FCSTD DOCUMENT  (FreeCAD 0.19R)
Label: horizontalBarCones
License: All rights reserved
LicenseURL: http://en.wikipedia.org/wiki/All_rights_reserved
objects: Mesh::Cone×6, Mesh::Cylinder×3

FEATURE [Mesh::Cone] Cone
  Closed = true
  EdgeLength = 1
  Length = 140
  Placement = pos=(0,0,0) rot=(0,-1,0;1.74533rad)
  Radius1 = 5
  Radius2 = 9
  Sampling = 50
FEATURE [Mesh::Cone] Cone001
  Closed = true
  EdgeLength = 1
  Length = 140
  Placement = pos=(60,0,0) rot=(0,1,0;4.88692rad)
  Radius1 = 5
  Radius2 = 9
  Sampling = 50
FEATURE [Mesh::Cylinder] Cylinder
  Closed = true
  EdgeLength = 1
  Length = 130
  Placement = pos=(-35,0,140) rot=(0,0,1;0rad)
  Radius = 9
  Sampling = 50
FEATURE [Mesh::Cone] Cone002
  Closed = true
  EdgeLength = 1
  Length = 60
  Placement = pos=(70,70,0) rot=(0,-1,0;1.74533rad)
  Radius1 = 3
  Radius2 = 5
  Sampling = 50
FEATURE [Mesh::Cone] Cone003
  Closed = true
  EdgeLength = 1
  Length = 60
  Placement = pos=(110,70,0) rot=(0,1,0;4.88692rad)
  Radius1 = 3
  Radius2 = 5
  Sampling = 50
FEATURE [Mesh::Cylinder] Cylinder001
  Closed = true
  EdgeLength = 1
  Length = 120
  Placement = pos=(30,70,60) rot=(0,0,1;0rad)
  Radius = 7
  Sampling = 50
FEATURE [Mesh::Cone] Cone004
  Closed = true
  EdgeLength = 1
  Length = 60
  Placement = pos=(70,110,0) rot=(0,-1,0;1.74533rad)
  Radius1 = 3
  Radius2 = 5
  Sampling = 50
FEATURE [Mesh::Cone] Cone005
  Closed = true
  EdgeLength = 1
  Length = 60
  Placement = pos=(110,110,0) rot=(0,1,0;4.88692rad)
  Radius1 = 3
  Radius2 = 5
  Sampling = 50
FEATURE [Mesh::Cylinder] Cylinder002
  Closed = true
  EdgeLength = 1
  Length = 120
  Placement = pos=(30,110,60) rot=(0,0,1;0rad)
  Radius = 7
  Sampling = 50
